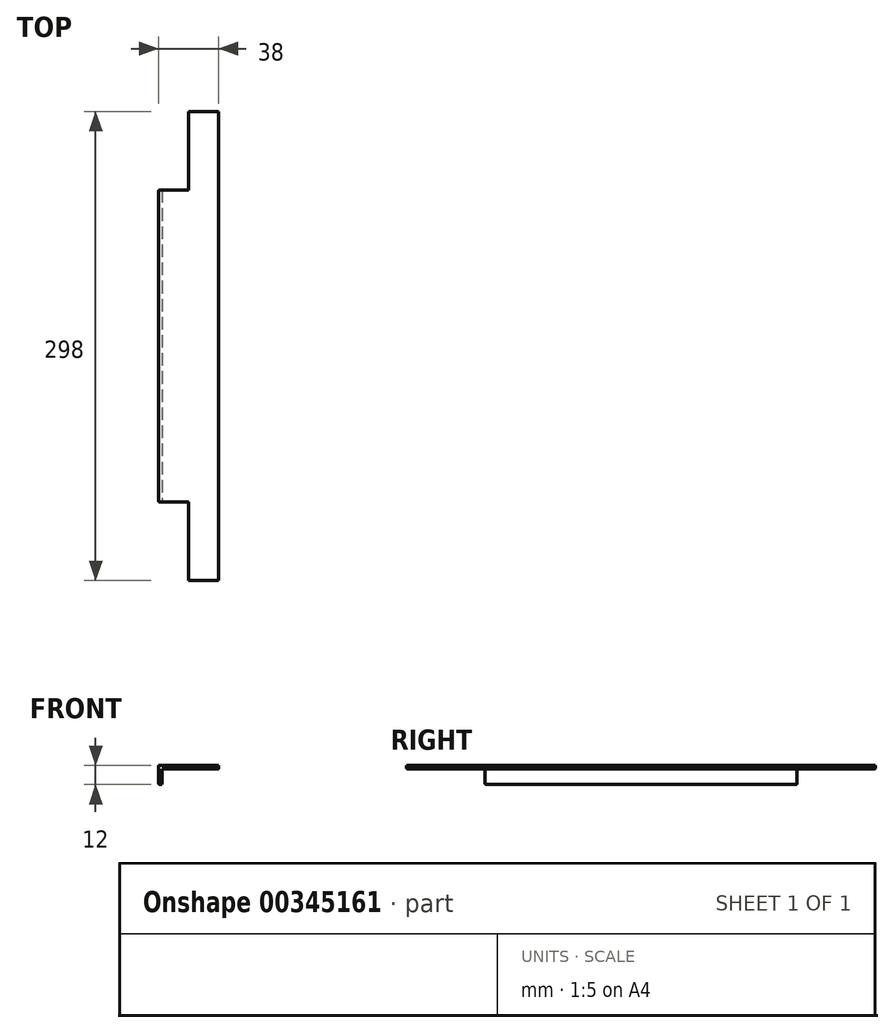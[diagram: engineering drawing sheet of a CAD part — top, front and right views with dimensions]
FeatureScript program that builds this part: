
annotation { "Feature Type Name" : "Feature", "Feature Type Description" : "" }
export const myFeature = defineFeature(function(context is Context, id is Id, definition is map)
    precondition{}
    {
        {
            var Q0;
            Q0=qCreatedBy(makeId("Right.planeOp"),FACE);
            var sketch = newSketch(context, id + "F0", { "sketchPlane" : qUnion([Q0])});
            skLineSegment(sketch, "E0.bottom", {"start": v(0, 0) * mm, "end": v(-38.54, 0) * mm});
            skLineSegment(sketch, "E0.top", {"start": v(0, 30.87) * mm, "end": v(-38.54, 30.87) * mm});
            skLineSegment(sketch, "E0.left", {"start": v(0, 0) * mm, "end": v(0, 30.87) * mm});
            skLineSegment(sketch, "E0.right", {"start": v(-38.54, 0) * mm, "end": v(-38.54, 30.87) * mm});
            skSolve(sketch);
        }
        {
            var Q0;
            Q0=makeQuery(id+"F0.imprint","IMPRINT",FACE,{"disambiguationData":[TD([[makeQuery(id+"F0.imprint","IMPRINT",EDGE,{"derivedFrom":sQuery(id+"F0.wireOp",EDGE,"E0.bottom")}),-1.0]])]});
            extrude(context, id + "F1", {"entities" : qUnion([Q0]), "oppositeDirection" : true, "depth" : 38 * mm});
        }
        {
            var Q0;
            Q0=makeQuery(id+"F1.opExtrude","SWEPT_FACE",FACE,{"disambiguationData":[OSD([sQuery(id+"F0.wireOp",EDGE,"E0.bottom")])]});
            extrude(context, id + "F2", {"entities" : qUnion([Q0]), "operationType" : NewBodyOperationType.INTERSECT, "oppositeDirection" : true, "depth" : 2 * mm});
        }
        {
            var Q0;
            Q0=makeQuery(id+"F1.opExtrude","SWEPT_FACE",FACE,{"disambiguationData":[OSD([sQuery(id+"F0.wireOp",EDGE,"E0.left")])]});
            extrude(context, id + "F3", {"entities" : qUnion([Q0]), "operationType" : NewBodyOperationType.ADD, "oppositeDirection" : true, "depth" : 298 * mm});
        }
        {
            var Q0;
            Q0=makeQuery(id+"F3.opExtrude","CAP_FACE",FACE,{"disambiguationData":[OSD([sQuery(id+"F0.wireOp",EDGE,"E0.left")])],"isStart":false});
            var sketch = newSketch(context, id + "F4", { "sketchPlane" : qUnion([Q0])});
            skLineSegment(sketch, "E1", {"start": v(-19, 2) * mm, "end": v(-19, 0) * mm});
            skSolve(sketch);
        }
        {
            var Q0;
            Q0=makeQuery(id+"F1.opExtrude","SWEPT_FACE",FACE,{"disambiguationData":[OSD([sQuery(id+"F0.wireOp",EDGE,"E0.left")])]});
            var sketch = newSketch(context, id + "F5", { "sketchPlane" : qUnion([Q0])});
            skLineSegment(sketch, "E2", {"start": v(19, 2) * mm, "end": v(19, 0) * mm});
            skSolve(sketch);
        }
        {
            var Q0;
            {var subQ0=sQuery(id+"F5.wireOp",EDGE,"E2");Q0=makeQuery(id+"F5.imprint","IMPRINT",FACE,{"disambiguationData":[TD([[makeQuery(id+"F5.imprint","IMPRINT",EDGE,{"derivedFrom":subQ0}),1.0]])]});}
            extrude(context, id + "F6", {"entities" : qUnion([Q0]), "operationType" : NewBodyOperationType.REMOVE, "oppositeDirection" : true, "depth" : 50 * mm});
        }
        {
            var Q0;
            {var subQ0=sQuery(id+"F4.wireOp",EDGE,"E1");Q0=makeQuery(id+"F4.imprint","IMPRINT",FACE,{"disambiguationData":[TD([[makeQuery(id+"F4.imprint","IMPRINT",EDGE,{"derivedFrom":subQ0}),-1.0]])]});}
            extrude(context, id + "F7", {"entities" : qUnion([Q0]), "operationType" : NewBodyOperationType.REMOVE, "oppositeDirection" : true, "depth" : 50 * mm});
        }
        {
            var Q0;
            {var subQ0=sQuery(id+"F0.wireOp",EDGE,"E0.left");var subQ1=sQuery(id+"F0.wireOp",EDGE,"E0.bottom");Q0=makeQuery(id+"F3.boolean.opBoolean","MERGE",FACE,{"derivedFrom":[makeQuery(id+"F1.opExtrude","SWEPT_FACE",FACE,{"disambiguationData":[OSD([subQ1])]}),makeQuery(id+"F3.opExtrude","SWEPT_FACE",FACE,{"disambiguationData":[OSD([subQ1,subQ0]),TDD([makeQuery(id+"F1.opExtrude","SWEPT_EDGE",EDGE,{"disambiguationData":[OSD([subQ1,subQ0])]})])]})]});}
            var sketch = newSketch(context, id + "F8", { "sketchPlane" : qUnion([Q0])});
            skLineSegment(sketch, "E3.bottom", {"start": v(-38, 50) * mm, "end": v(-33.11, 50) * mm});
            skLineSegment(sketch, "E3.top", {"start": v(-38, 248) * mm, "end": v(-33.11, 248) * mm});
            skLineSegment(sketch, "E3.left", {"start": v(-38, 50) * mm, "end": v(-38, 248) * mm});
            skLineSegment(sketch, "E3.right", {"start": v(-33.11, 50) * mm, "end": v(-33.11, 248) * mm});
            skSolve(sketch);
        }
        {
            var Q0;
            Q0=makeQuery(id+"F8.imprint","IMPRINT",FACE,{"disambiguationData":[TD([[makeQuery(id+"F8.imprint","IMPRINT",EDGE,{"derivedFrom":sQuery(id+"F8.wireOp",EDGE,"E3.bottom")}),1.0]])]});
            extrude(context, id + "F9", {"entities" : qUnion([Q0]), "operationType" : NewBodyOperationType.ADD, "depth" : 10 * mm});
        }
        {
            var Q0;
            Q0=makeQuery(id+"F9.opExtrude","SWEPT_FACE",FACE,{"disambiguationData":[OSD([sQuery(id+"F8.wireOp",EDGE,"E3.right")])]});
            extrude(context, id + "F10", {"entities" : qUnion([Q0]), "operationType" : NewBodyOperationType.REMOVE, "oppositeDirection" : true, "depth" : 2.9 * mm});
        }
        {
            var Q0;
            {var subQ0=sQuery(id+"F0.wireOp",EDGE,"E0.left");var subQ1=sQuery(id+"F0.wireOp",EDGE,"E0.bottom");Q0=makeQuery(id+"F3.opExtrude","CAP_EDGE",EDGE,{"disambiguationData":[OSD([subQ1,subQ0]),TDD([makeQuery(id+"F2.boolean.opBoolean","COPY",EDGE,{"derivedFrom":makeQuery(id+"F2.boolean.toolComplement.opBoolean","COPY",EDGE,{"derivedFrom":makeQuery(id+"F2.opExtrude","CAP_EDGE",EDGE,{"disambiguationData":[OSD([subQ1,subQ0])],"isStart":false})})})])],"isStart":false});}
            var Q1;
            {var subQ0=sQuery(id+"F0.wireOp",EDGE,"E0.left");var subQ1=sQuery(id+"F0.wireOp",EDGE,"E0.bottom");Q1=makeQuery(id+"F3.opExtrude","CAP_EDGE",EDGE,{"disambiguationData":[OSD([subQ1,subQ0]),TDD([makeQuery(id+"F1.opExtrude","SWEPT_EDGE",EDGE,{"disambiguationData":[OSD([subQ1,subQ0])]})])],"isStart":false});}
            var Q2;
            Q2=makeQuery(id+"F7.boolean.opBoolean","COPY",EDGE,{"derivedFrom":makeQuery(id+"F7.opExtrude","CAP_EDGE",EDGE,{"disambiguationData":[OSD([sQuery(id+"F4.wireOp",EDGE,"E1")])],"isStart":true})});
            var Q3;
            {var subQ0=sQuery(id+"F4.wireOp",EDGE,"E1");var subQ1=sQuery(id+"F0.wireOp",EDGE,"E0.left");var subQ2=sQuery(id+"F0.wireOp",EDGE,"E0.bottom");Q3=makeQuery(id+"F7.boolean.opBoolean","COPY",EDGE,{"derivedFrom":makeQuery(id+"F7.opExtrude","SWEPT_EDGE",EDGE,{"disambiguationData":[OSD([subQ2,subQ1,subQ0]),TDD([makeQuery(id+"F4.imprint","INTERSECT",VERTEX,{"derivedFrom":[makeQuery(id+"F3.opExtrude","CAP_EDGE",EDGE,{"disambiguationData":[OSD([subQ2,subQ1]),TDD([makeQuery(id+"F2.boolean.opBoolean","COPY",EDGE,{"derivedFrom":makeQuery(id+"F2.boolean.toolComplement.opBoolean","COPY",EDGE,{"derivedFrom":makeQuery(id+"F2.opExtrude","CAP_EDGE",EDGE,{"disambiguationData":[OSD([subQ2,subQ1])],"isStart":false})})})])],"isStart":false}),subQ0]})])]})});}
            var Q4;
            {var subQ0=sQuery(id+"F4.wireOp",EDGE,"E1");var subQ1=sQuery(id+"F0.wireOp",EDGE,"E0.left");var subQ2=sQuery(id+"F0.wireOp",EDGE,"E0.bottom");Q4=makeQuery(id+"F7.boolean.opBoolean","COPY",EDGE,{"derivedFrom":makeQuery(id+"F7.opExtrude","SWEPT_EDGE",EDGE,{"disambiguationData":[OSD([subQ2,subQ1,subQ0]),TDD([makeQuery(id+"F4.imprint","INTERSECT",VERTEX,{"derivedFrom":[makeQuery(id+"F3.opExtrude","CAP_EDGE",EDGE,{"disambiguationData":[OSD([subQ2,subQ1]),TDD([makeQuery(id+"F1.opExtrude","SWEPT_EDGE",EDGE,{"disambiguationData":[OSD([subQ2,subQ1])]})])],"isStart":false}),subQ0]})])]})});}
            var Q5;
            {var subQ0=sQuery(id+"F0.wireOp",EDGE,"E0.left");var subQ1=sQuery(id+"F0.wireOp",EDGE,"E0.bottom");var subQ2=makeQuery(id+"F3.opExtrude","CAP_EDGE",EDGE,{"disambiguationData":[OSD([subQ1,subQ0]),TDD([makeQuery(id+"F2.boolean.opBoolean","COPY",EDGE,{"derivedFrom":makeQuery(id+"F2.boolean.toolComplement.opBoolean","COPY",EDGE,{"derivedFrom":makeQuery(id+"F2.opExtrude","CAP_EDGE",EDGE,{"disambiguationData":[OSD([subQ1,subQ0])],"isStart":false})})})])],"isStart":false});Q5=makeQuery(id+"F7.boolean.opBoolean","COPY",EDGE,{"derivedFrom":makeQuery(id+"F7.opExtrude","CAP_EDGE",EDGE,{"disambiguationData":[OSD([subQ1,subQ0]),TDD([makeQuery(id+"F4.imprint","IMPRINT",EDGE,{"disambiguationData":[TD([[makeQuery(id+"F4.imprint","INTERSECT",VERTEX,{"derivedFrom":[subQ2,sQuery(id+"F4.wireOp",EDGE,"E1")]}),1.0]])],"derivedFrom":subQ2})])],"isStart":false})});}
            var Q6;
            {var subQ0=sQuery(id+"F8.wireOp",EDGE,"E3.right");var subQ1=sQuery(id+"F8.wireOp",EDGE,"E3.top");var subQ2=sQuery(id+"F0.wireOp",EDGE,"E0.left");var subQ3=sQuery(id+"F0.wireOp",EDGE,"E0.bottom");var subQ4=makeQuery(id+"F3.opExtrude","CAP_EDGE",EDGE,{"disambiguationData":[OSD([subQ3,subQ2]),TDD([makeQuery(id+"F1.opExtrude","SWEPT_EDGE",EDGE,{"disambiguationData":[OSD([subQ3,subQ2])]})])],"isStart":false});Q6=makeQuery(id+"F10.boolean.opBoolean","MERGE",EDGE,{"derivedFrom":[makeQuery(id+"F7.boolean.opBoolean","COPY",EDGE,{"derivedFrom":makeQuery(id+"F7.opExtrude","CAP_EDGE",EDGE,{"disambiguationData":[OSD([subQ3,subQ2]),TDD([makeQuery(id+"F4.imprint","IMPRINT",EDGE,{"disambiguationData":[TD([[makeQuery(id+"F4.imprint","INTERSECT",VERTEX,{"derivedFrom":[subQ4,sQuery(id+"F4.wireOp",EDGE,"E1")]}),1.0]])],"derivedFrom":subQ4})])],"isStart":false})}),makeQuery(id+"F10.opExtrude","SWEPT_EDGE",EDGE,{"disambiguationData":[OSD([subQ3,subQ2,subQ1,subQ0]),TDD([makeQuery(id+"F9.opExtrude","CAP_VERTEX",VERTEX,{"disambiguationData":[OSD([subQ3,subQ2,subQ1,subQ0])],"isStart":true})])]})]});}
            var Q7;
            Q7=makeQuery(id+"F9.boolean.opBoolean","MERGE",EDGE,{"derivedFrom":[makeQuery(id+"F7.boolean.opBoolean","COPY",EDGE,{"derivedFrom":makeQuery(id+"F7.opExtrude","CAP_EDGE",EDGE,{"disambiguationData":[OSD([sQuery(id+"F0.wireOp",EDGE,"E0.left")])],"isStart":false})}),makeQuery(id+"F9.opExtrude","SWEPT_EDGE",EDGE,{"disambiguationData":[OSD([sQuery(id+"F8.wireOp",EDGE,"E3.top"),sQuery(id+"F8.wireOp",EDGE,"E3.left")])]})]});
            var Q8;
            Q8=makeQuery(id+"F10.boolean.opBoolean","COPY",EDGE,{"derivedFrom":makeQuery(id+"F10.opExtrude","CAP_EDGE",EDGE,{"disambiguationData":[OSD([sQuery(id+"F0.wireOp",EDGE,"E0.bottom"),sQuery(id+"F0.wireOp",EDGE,"E0.left"),sQuery(id+"F8.wireOp",EDGE,"E3.top"),sQuery(id+"F8.wireOp",EDGE,"E3.right")])],"isStart":false})});
            var Q9;
            Q9=makeQuery(id+"F9.opExtrude","CAP_EDGE",EDGE,{"disambiguationData":[OSD([sQuery(id+"F8.wireOp",EDGE,"E3.top")])],"isStart":false});
            var Q10;
            Q10=makeQuery(id+"F7.boolean.opBoolean","COPY",EDGE,{"derivedFrom":makeQuery(id+"F7.opExtrude","CAP_EDGE",EDGE,{"disambiguationData":[OSD([sQuery(id+"F4.wireOp",EDGE,"E1")])],"isStart":false})});
            var Q11;
            {var subQ0=sQuery(id+"F0.wireOp",EDGE,"E0.left");var subQ1=sQuery(id+"F0.wireOp",EDGE,"E0.bottom");Q11=makeQuery(id+"F3.boolean.opBoolean","MERGE",EDGE,{"derivedFrom":[makeQuery(id+"F2.boolean.opBoolean","COPY",EDGE,{"derivedFrom":makeQuery(id+"F2.boolean.toolComplement.opBoolean","COPY",EDGE,{"derivedFrom":makeQuery(id+"F2.opExtrude","CAP_EDGE",EDGE,{"disambiguationData":[OSD([subQ1]),TDD([makeQuery(id+"F1.opExtrude","CAP_EDGE",EDGE,{"disambiguationData":[OSD([subQ1])],"isStart":false})])],"isStart":false})})}),makeQuery(id+"F3.opExtrude","SWEPT_EDGE",EDGE,{"disambiguationData":[OSD([subQ1,subQ0]),TDD([makeQuery(id+"F2.boolean.opBoolean","COPY",VERTEX,{"derivedFrom":makeQuery(id+"F2.boolean.toolComplement.opBoolean","COPY",VERTEX,{"derivedFrom":makeQuery(id+"F2.opExtrude","CAP_VERTEX",VERTEX,{"disambiguationData":[OSD([subQ1,subQ0]),TDD([makeQuery(id+"F1.opExtrude","CAP_VERTEX",VERTEX,{"disambiguationData":[OSD([subQ1,subQ0])],"isStart":false})])],"isStart":false})})})])]})]});}
            var Q12;
            Q12=makeQuery(id+"F9.opExtrude","CAP_EDGE",EDGE,{"disambiguationData":[OSD([sQuery(id+"F8.wireOp",EDGE,"E3.left")])],"isStart":false});
            var Q13;
            {var subQ0=sQuery(id+"F8.wireOp",EDGE,"E3.right");Q13=makeQuery(id+"F10.boolean.opBoolean","COPY",EDGE,{"derivedFrom":makeQuery(id+"F10.opExtrude","CAP_EDGE",EDGE,{"disambiguationData":[OSD([subQ0]),TDD([makeQuery(id+"F9.opExtrude","CAP_EDGE",EDGE,{"disambiguationData":[OSD([subQ0])],"isStart":false})])],"isStart":false})});}
            var Q14;
            Q14=makeQuery(id+"F9.opExtrude","CAP_EDGE",EDGE,{"disambiguationData":[OSD([sQuery(id+"F8.wireOp",EDGE,"E3.bottom")])],"isStart":false});
            var Q15;
            Q15=makeQuery(id+"F9.boolean.opBoolean","MERGE",EDGE,{"derivedFrom":[makeQuery(id+"F6.boolean.opBoolean","COPY",EDGE,{"derivedFrom":makeQuery(id+"F6.opExtrude","CAP_EDGE",EDGE,{"disambiguationData":[OSD([sQuery(id+"F0.wireOp",EDGE,"E0.left")])],"isStart":false})}),makeQuery(id+"F9.opExtrude","SWEPT_EDGE",EDGE,{"disambiguationData":[OSD([sQuery(id+"F8.wireOp",EDGE,"E3.bottom"),sQuery(id+"F8.wireOp",EDGE,"E3.left")])]})]});
            var Q16;
            Q16=makeQuery(id+"F10.boolean.opBoolean","COPY",EDGE,{"derivedFrom":makeQuery(id+"F10.opExtrude","CAP_EDGE",EDGE,{"disambiguationData":[OSD([sQuery(id+"F0.wireOp",EDGE,"E0.bottom"),sQuery(id+"F0.wireOp",EDGE,"E0.left"),sQuery(id+"F8.wireOp",EDGE,"E3.bottom"),sQuery(id+"F8.wireOp",EDGE,"E3.right")])],"isStart":false})});
            var Q17;
            {var subQ0=sQuery(id+"F8.wireOp",EDGE,"E3.right");var subQ1=sQuery(id+"F8.wireOp",EDGE,"E3.bottom");var subQ2=sQuery(id+"F0.wireOp",EDGE,"E0.left");var subQ3=sQuery(id+"F0.wireOp",EDGE,"E0.bottom");var subQ4=makeQuery(id+"F1.opExtrude","SWEPT_EDGE",EDGE,{"disambiguationData":[OSD([subQ3,subQ2])]});Q17=makeQuery(id+"F10.boolean.opBoolean","MERGE",EDGE,{"derivedFrom":[makeQuery(id+"F6.boolean.opBoolean","COPY",EDGE,{"derivedFrom":makeQuery(id+"F6.opExtrude","CAP_EDGE",EDGE,{"disambiguationData":[OSD([subQ3,subQ2]),TDD([makeQuery(id+"F5.imprint","IMPRINT",EDGE,{"disambiguationData":[TD([[makeQuery(id+"F5.imprint","INTERSECT",VERTEX,{"derivedFrom":[subQ4,makeQuery(id+"F1.opExtrude","CAP_EDGE",EDGE,{"disambiguationData":[OSD([subQ2])],"isStart":false})]}),-1.0]])],"derivedFrom":subQ4})])],"isStart":false})}),makeQuery(id+"F10.opExtrude","SWEPT_EDGE",EDGE,{"disambiguationData":[OSD([subQ3,subQ2,subQ1,subQ0]),TDD([makeQuery(id+"F9.opExtrude","CAP_VERTEX",VERTEX,{"disambiguationData":[OSD([subQ3,subQ2,subQ1,subQ0])],"isStart":true})])]})]});}
            var Q18;
            {var subQ0=sQuery(id+"F0.wireOp",EDGE,"E0.left");var subQ1=sQuery(id+"F0.wireOp",EDGE,"E0.bottom");var subQ2=makeQuery(id+"F2.boolean.opBoolean","COPY",EDGE,{"derivedFrom":makeQuery(id+"F2.boolean.toolComplement.opBoolean","COPY",EDGE,{"derivedFrom":makeQuery(id+"F2.opExtrude","CAP_EDGE",EDGE,{"disambiguationData":[OSD([subQ1,subQ0])],"isStart":false})})});Q18=makeQuery(id+"F6.boolean.opBoolean","COPY",EDGE,{"derivedFrom":makeQuery(id+"F6.opExtrude","CAP_EDGE",EDGE,{"disambiguationData":[OSD([subQ1,subQ0]),TDD([makeQuery(id+"F5.imprint","IMPRINT",EDGE,{"disambiguationData":[TD([[makeQuery(id+"F5.imprint","INTERSECT",VERTEX,{"derivedFrom":[subQ2,makeQuery(id+"F1.opExtrude","CAP_EDGE",EDGE,{"disambiguationData":[OSD([subQ0])],"isStart":false})]}),-1.0]])],"derivedFrom":subQ2})])],"isStart":false})});}
            var Q19;
            Q19=makeQuery(id+"F6.boolean.opBoolean","COPY",EDGE,{"derivedFrom":makeQuery(id+"F6.opExtrude","CAP_EDGE",EDGE,{"disambiguationData":[OSD([sQuery(id+"F5.wireOp",EDGE,"E2")])],"isStart":false})});
            var Q20;
            {var subQ0=sQuery(id+"F5.wireOp",EDGE,"E2");var subQ1=sQuery(id+"F0.wireOp",EDGE,"E0.left");var subQ2=sQuery(id+"F0.wireOp",EDGE,"E0.bottom");Q20=makeQuery(id+"F6.boolean.opBoolean","COPY",EDGE,{"derivedFrom":makeQuery(id+"F6.opExtrude","SWEPT_EDGE",EDGE,{"disambiguationData":[OSD([subQ2,subQ1,subQ0]),TDD([makeQuery(id+"F5.imprint","INTERSECT",VERTEX,{"derivedFrom":[makeQuery(id+"F2.boolean.opBoolean","COPY",EDGE,{"derivedFrom":makeQuery(id+"F2.boolean.toolComplement.opBoolean","COPY",EDGE,{"derivedFrom":makeQuery(id+"F2.opExtrude","CAP_EDGE",EDGE,{"disambiguationData":[OSD([subQ2,subQ1])],"isStart":false})})}),subQ0]})])]})});}
            var Q21;
            {var subQ0=sQuery(id+"F5.wireOp",EDGE,"E2");var subQ1=sQuery(id+"F0.wireOp",EDGE,"E0.left");var subQ2=sQuery(id+"F0.wireOp",EDGE,"E0.bottom");Q21=makeQuery(id+"F6.boolean.opBoolean","COPY",EDGE,{"derivedFrom":makeQuery(id+"F6.opExtrude","SWEPT_EDGE",EDGE,{"disambiguationData":[OSD([subQ2,subQ1,subQ0]),TDD([makeQuery(id+"F5.imprint","INTERSECT",VERTEX,{"derivedFrom":[makeQuery(id+"F1.opExtrude","SWEPT_EDGE",EDGE,{"disambiguationData":[OSD([subQ2,subQ1])]}),subQ0]})])]})});}
            var Q22;
            Q22=makeQuery(id+"F2.boolean.opBoolean","COPY",EDGE,{"derivedFrom":makeQuery(id+"F2.boolean.toolComplement.opBoolean","COPY",EDGE,{"derivedFrom":makeQuery(id+"F2.opExtrude","CAP_EDGE",EDGE,{"disambiguationData":[OSD([sQuery(id+"F0.wireOp",EDGE,"E0.bottom"),sQuery(id+"F0.wireOp",EDGE,"E0.left")])],"isStart":false})})});
            var Q23;
            Q23=makeQuery(id+"F1.opExtrude","SWEPT_EDGE",EDGE,{"disambiguationData":[OSD([sQuery(id+"F0.wireOp",EDGE,"E0.bottom"),sQuery(id+"F0.wireOp",EDGE,"E0.left")])]});
            var Q24;
            Q24=makeQuery(id+"F6.boolean.opBoolean","COPY",EDGE,{"derivedFrom":makeQuery(id+"F6.opExtrude","CAP_EDGE",EDGE,{"disambiguationData":[OSD([sQuery(id+"F5.wireOp",EDGE,"E2")])],"isStart":true})});
            fillet(context, id + "F11", {"entities" : qUnion([Q0, Q1, Q2, Q3, Q4, Q5, Q6, Q7, Q8, Q9, Q10, Q11, Q12, Q13, Q14, Q15, Q16, Q17, Q18, Q19, Q20, Q21, Q22, Q23, Q24]), "radius" : 0.5 * mm, "tangentPropagation" : true, "allowEdgeOverflow" : false});
        }
    });
